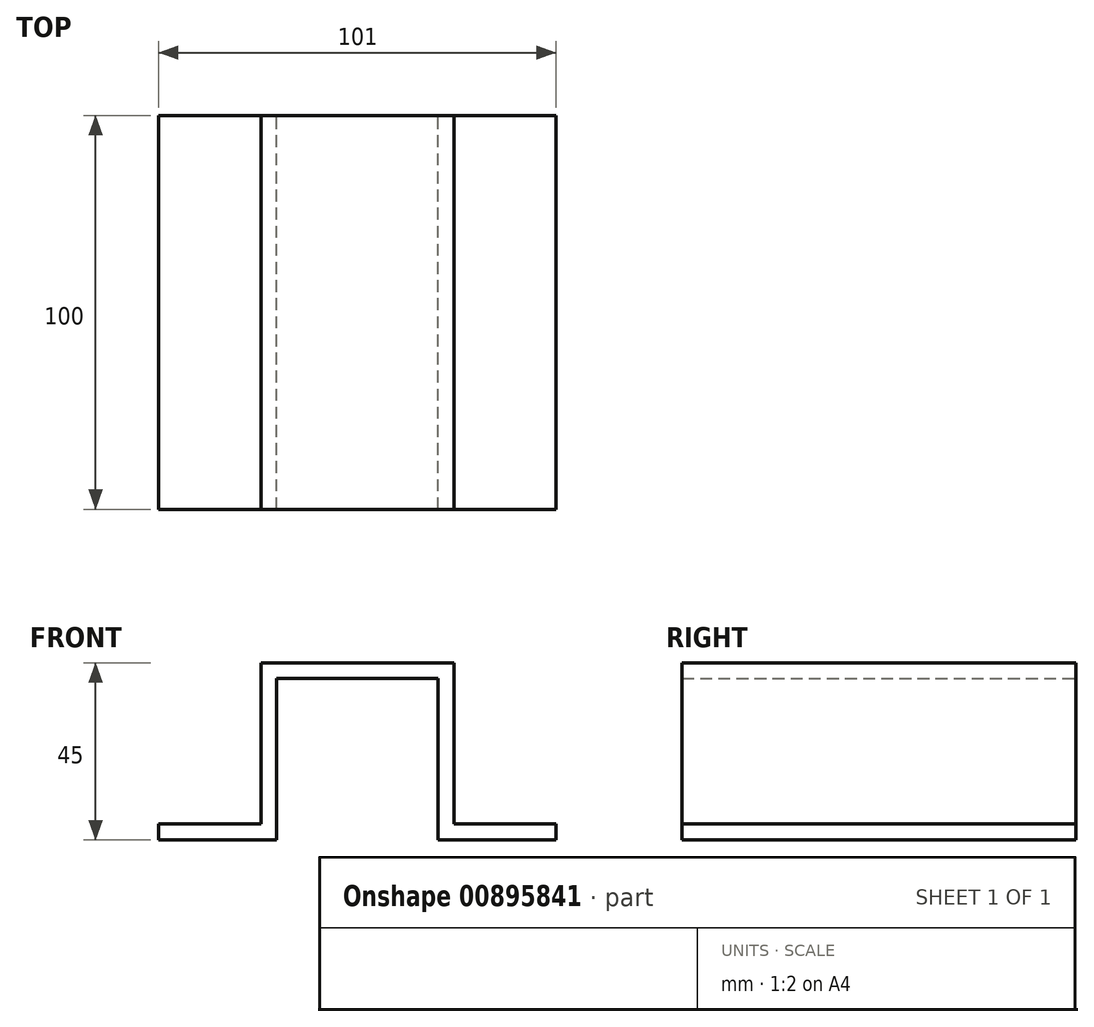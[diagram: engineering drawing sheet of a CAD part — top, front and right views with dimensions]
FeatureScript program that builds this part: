
annotation { "Feature Type Name" : "Feature", "Feature Type Description" : "" }
export const myFeature = defineFeature(function(context is Context, id is Id, definition is map)
    precondition{}
    {
        {
            var Q0;
            Q0=qCreatedBy(makeId("Front.planeOp"),FACE);
            var sketch = newSketch(context, id + "F0", { "sketchPlane" : qUnion([Q0])});
            skLineSegment(sketch, "E0", {"start": v(-41.73, 0) * mm, "end": v(-11.73, 0) * mm});
            skLineSegment(sketch, "E1", {"start": v(-11.73, 0) * mm, "end": v(-11.73, 41) * mm});
            skLineSegment(sketch, "E2", {"start": v(-11.73, 41) * mm, "end": v(29.27, 41) * mm});
            skLineSegment(sketch, "E3", {"start": v(29.27, 41) * mm, "end": v(29.27, 0) * mm});
            skLineSegment(sketch, "E4", {"start": v(29.27, 0) * mm, "end": v(59.27, 0) * mm});
            skLineSegment(sketch, "E5", {"start": v(59.27, 0) * mm, "end": v(59.27, 4) * mm});
            skLineSegment(sketch, "E6", {"start": v(59.27, 4) * mm, "end": v(33.27, 4) * mm});
            skLineSegment(sketch, "E7", {"start": v(33.27, 4) * mm, "end": v(33.27, 45) * mm});
            skLineSegment(sketch, "E8", {"start": v(33.27, 45) * mm, "end": v(-15.73, 45) * mm});
            skLineSegment(sketch, "E9", {"start": v(-15.73, 45) * mm, "end": v(-15.73, 4) * mm});
            skLineSegment(sketch, "E10", {"start": v(-15.73, 4) * mm, "end": v(-41.73, 4) * mm});
            skLineSegment(sketch, "E11", {"start": v(-41.73, 4) * mm, "end": v(-41.73, 0) * mm});
            skSolve(sketch);
        }
        {
            var Q0;
            Q0 = qSketchRegion(id + "F0", true);
            extrude(context, id + "F1", {"entities" : qUnion([Q0]), "depth" : 100 * mm, "offsetDistance" : 25 * mm});
        }
    });
